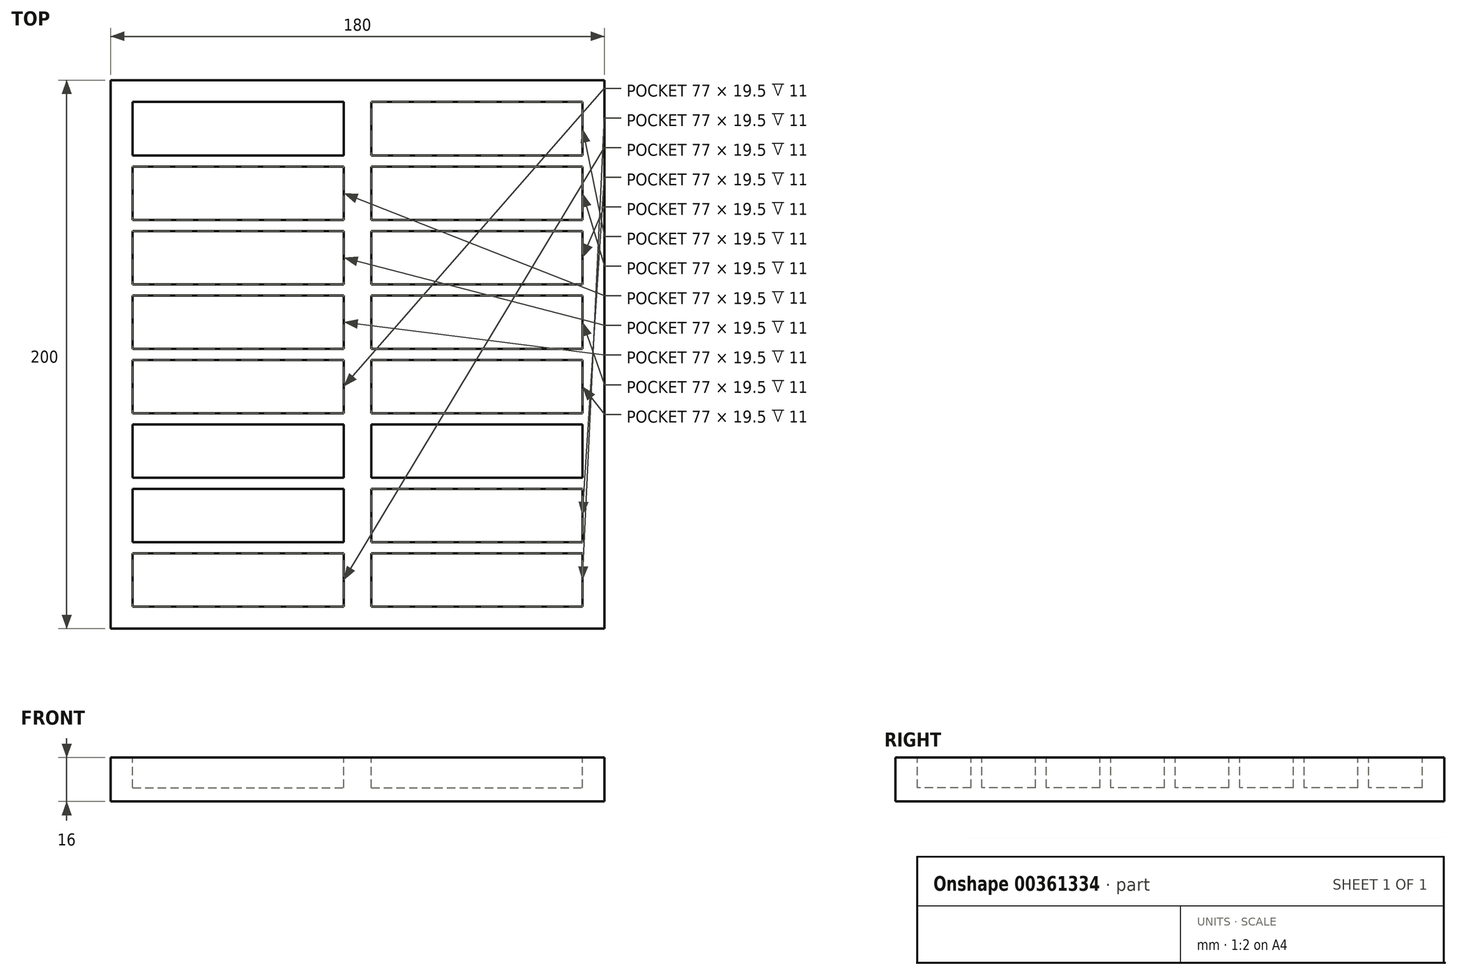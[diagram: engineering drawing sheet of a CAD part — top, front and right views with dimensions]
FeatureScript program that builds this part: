
annotation { "Feature Type Name" : "Feature", "Feature Type Description" : "" }
export const myFeature = defineFeature(function(context is Context, id is Id, definition is map)
    precondition{}
    {
        {
            var Q0;
            Q0=qCreatedBy(makeId("Top.planeOp"),FACE);
            var sketch = newSketch(context, id + "F0", { "sketchPlane" : qUnion([Q0])});
            skLineSegment(sketch, "E0.bottom", {"start": v(90, 100) * mm, "end": v(-90, 100) * mm});
            skLineSegment(sketch, "E0.top", {"start": v(90, -100) * mm, "end": v(-90, -100) * mm});
            skLineSegment(sketch, "E0.left", {"start": v(90, 100) * mm, "end": v(90, -100) * mm});
            skLineSegment(sketch, "E0.right", {"start": v(-90, 100) * mm, "end": v(-90, -100) * mm});
            skPoint(sketch, "E0.middle", {"position": v(0, 0) * mm});
            skSolve(sketch);
        }
        {
            var Q0;
            Q0 = qSketchRegion(id + "F0", true);
            extrude(context, id + "F1", {"entities" : qUnion([Q0]), "depth" : 16 * mm});
        }
        {
            var Q0;
            Q0=makeQuery(id+"F1.opExtrude","CAP_FACE",FACE,{"disambiguationData":[OSD([sQuery(id+"F0.wireOp",EDGE,"E0.bottom"),sQuery(id+"F0.wireOp",EDGE,"E0.top"),sQuery(id+"F0.wireOp",EDGE,"E0.left"),sQuery(id+"F0.wireOp",EDGE,"E0.right")])],"isStart":false});
            var sketch = newSketch(context, id + "F2", { "sketchPlane" : qUnion([Q0])});
            skLineSegment(sketch, "E1.bottom", {"start": v(-82, 92) * mm, "end": v(-5, 92) * mm});
            skLineSegment(sketch, "E1.top", {"start": v(-82, 72.5) * mm, "end": v(-5, 72.5) * mm});
            skLineSegment(sketch, "E1.left", {"start": v(-82, 92) * mm, "end": v(-82, 72.5) * mm});
            skLineSegment(sketch, "E1.right", {"start": v(-5, 92) * mm, "end": v(-5, 72.5) * mm});
            skLineSegment(sketch, "E2.0.1.0", {"start": v(-82, 49) * mm, "end": v(-5, 49) * mm});
            skLineSegment(sketch, "E2.0.1.1", {"start": v(-5, 68.5) * mm, "end": v(-5, 49) * mm});
            skLineSegment(sketch, "E2.0.1.2", {"start": v(-82, 68.5) * mm, "end": v(-5, 68.5) * mm});
            skLineSegment(sketch, "E2.0.1.3", {"start": v(-82, 68.5) * mm, "end": v(-82, 49) * mm});
            skLineSegment(sketch, "E2.0.2.0", {"start": v(-82, 25.5) * mm, "end": v(-5, 25.5) * mm});
            skLineSegment(sketch, "E2.0.2.1", {"start": v(-5, 45) * mm, "end": v(-5, 25.5) * mm});
            skLineSegment(sketch, "E2.0.2.2", {"start": v(-82, 45) * mm, "end": v(-5, 45) * mm});
            skLineSegment(sketch, "E2.0.2.3", {"start": v(-82, 45) * mm, "end": v(-82, 25.5) * mm});
            skLineSegment(sketch, "E2.0.3.0", {"start": v(-82, 2) * mm, "end": v(-5, 2) * mm});
            skLineSegment(sketch, "E2.0.3.1", {"start": v(-5, 21.5) * mm, "end": v(-5, 2) * mm});
            skLineSegment(sketch, "E2.0.3.2", {"start": v(-82, 21.5) * mm, "end": v(-5, 21.5) * mm});
            skLineSegment(sketch, "E2.0.3.3", {"start": v(-82, 21.5) * mm, "end": v(-82, 2) * mm});
            skLineSegment(sketch, "E2.0.4.0", {"start": v(-82, -21.5) * mm, "end": v(-5, -21.5) * mm});
            skLineSegment(sketch, "E2.0.4.1", {"start": v(-5, -2) * mm, "end": v(-5, -21.5) * mm});
            skLineSegment(sketch, "E2.0.4.2", {"start": v(-82, -2) * mm, "end": v(-5, -2) * mm});
            skLineSegment(sketch, "E2.0.4.3", {"start": v(-82, -2) * mm, "end": v(-82, -21.5) * mm});
            skLineSegment(sketch, "E2.0.5.0", {"start": v(-82, -45) * mm, "end": v(-5, -45) * mm});
            skLineSegment(sketch, "E2.0.5.1", {"start": v(-5, -25.5) * mm, "end": v(-5, -45) * mm});
            skLineSegment(sketch, "E2.0.5.2", {"start": v(-82, -25.5) * mm, "end": v(-5, -25.5) * mm});
            skLineSegment(sketch, "E2.0.5.3", {"start": v(-82, -25.5) * mm, "end": v(-82, -45) * mm});
            skLineSegment(sketch, "E2.0.6.0", {"start": v(-82, -68.5) * mm, "end": v(-5, -68.5) * mm});
            skLineSegment(sketch, "E2.0.6.1", {"start": v(-5, -49) * mm, "end": v(-5, -68.5) * mm});
            skLineSegment(sketch, "E2.0.6.2", {"start": v(-82, -49) * mm, "end": v(-5, -49) * mm});
            skLineSegment(sketch, "E2.0.6.3", {"start": v(-82, -49) * mm, "end": v(-82, -68.5) * mm});
            skLineSegment(sketch, "E2.0.7.0", {"start": v(-82, -92) * mm, "end": v(-5, -92) * mm});
            skLineSegment(sketch, "E2.0.7.1", {"start": v(-5, -72.5) * mm, "end": v(-5, -92) * mm});
            skLineSegment(sketch, "E2.0.7.2", {"start": v(-82, -72.5) * mm, "end": v(-5, -72.5) * mm});
            skLineSegment(sketch, "E2.0.7.3", {"start": v(-82, -72.5) * mm, "end": v(-82, -92) * mm});
            skLineSegment(sketch, "E2.1.0.0", {"start": v(5, 72.5) * mm, "end": v(82, 72.5) * mm});
            skLineSegment(sketch, "E2.1.0.1", {"start": v(82, 92) * mm, "end": v(82, 72.5) * mm});
            skLineSegment(sketch, "E2.1.0.2", {"start": v(5, 92) * mm, "end": v(82, 92) * mm});
            skLineSegment(sketch, "E2.1.0.3", {"start": v(5, 92) * mm, "end": v(5, 72.5) * mm});
            skLineSegment(sketch, "E2.1.1.0", {"start": v(5, 49) * mm, "end": v(82, 49) * mm});
            skLineSegment(sketch, "E2.1.1.1", {"start": v(82, 68.5) * mm, "end": v(82, 49) * mm});
            skLineSegment(sketch, "E2.1.1.2", {"start": v(5, 68.5) * mm, "end": v(82, 68.5) * mm});
            skLineSegment(sketch, "E2.1.1.3", {"start": v(5, 68.5) * mm, "end": v(5, 49) * mm});
            skLineSegment(sketch, "E2.1.2.0", {"start": v(5, 25.5) * mm, "end": v(82, 25.5) * mm});
            skLineSegment(sketch, "E2.1.2.1", {"start": v(82, 45) * mm, "end": v(82, 25.5) * mm});
            skLineSegment(sketch, "E2.1.2.2", {"start": v(5, 45) * mm, "end": v(82, 45) * mm});
            skLineSegment(sketch, "E2.1.2.3", {"start": v(5, 45) * mm, "end": v(5, 25.5) * mm});
            skLineSegment(sketch, "E2.1.3.0", {"start": v(5, 2) * mm, "end": v(82, 2) * mm});
            skLineSegment(sketch, "E2.1.3.1", {"start": v(82, 21.5) * mm, "end": v(82, 2) * mm});
            skLineSegment(sketch, "E2.1.3.2", {"start": v(5, 21.5) * mm, "end": v(82, 21.5) * mm});
            skLineSegment(sketch, "E2.1.3.3", {"start": v(5, 21.5) * mm, "end": v(5, 2) * mm});
            skLineSegment(sketch, "E2.1.4.0", {"start": v(5, -21.5) * mm, "end": v(82, -21.5) * mm});
            skLineSegment(sketch, "E2.1.4.1", {"start": v(82, -2) * mm, "end": v(82, -21.5) * mm});
            skLineSegment(sketch, "E2.1.4.2", {"start": v(5, -2) * mm, "end": v(82, -2) * mm});
            skLineSegment(sketch, "E2.1.4.3", {"start": v(5, -2) * mm, "end": v(5, -21.5) * mm});
            skLineSegment(sketch, "E2.1.5.0", {"start": v(5, -45) * mm, "end": v(82, -45) * mm});
            skLineSegment(sketch, "E2.1.5.1", {"start": v(82, -25.5) * mm, "end": v(82, -45) * mm});
            skLineSegment(sketch, "E2.1.5.2", {"start": v(5, -25.5) * mm, "end": v(82, -25.5) * mm});
            skLineSegment(sketch, "E2.1.5.3", {"start": v(5, -25.5) * mm, "end": v(5, -45) * mm});
            skLineSegment(sketch, "E2.1.6.0", {"start": v(5, -68.5) * mm, "end": v(82, -68.5) * mm});
            skLineSegment(sketch, "E2.1.6.1", {"start": v(82, -49) * mm, "end": v(82, -68.5) * mm});
            skLineSegment(sketch, "E2.1.6.2", {"start": v(5, -49) * mm, "end": v(82, -49) * mm});
            skLineSegment(sketch, "E2.1.6.3", {"start": v(5, -49) * mm, "end": v(5, -68.5) * mm});
            skLineSegment(sketch, "E2.1.7.0", {"start": v(5, -92) * mm, "end": v(82, -92) * mm});
            skLineSegment(sketch, "E2.1.7.1", {"start": v(82, -72.5) * mm, "end": v(82, -92) * mm});
            skLineSegment(sketch, "E2.1.7.2", {"start": v(5, -72.5) * mm, "end": v(82, -72.5) * mm});
            skLineSegment(sketch, "E2.1.7.3", {"start": v(5, -72.5) * mm, "end": v(5, -92) * mm});
            skLineSegment(sketch, "E2.direction1", {"start": v(-82, 72.5) * mm, "end": v(5, 72.5) * mm, "construction": true});
            skLineSegment(sketch, "E2.direction2", {"start": v(-82, 72.5) * mm, "end": v(-82, 49) * mm, "construction": true});
            skSolve(sketch);
        }
        {
            var Q0;
            Q0=makeQuery(id+"F2.imprint","IMPRINT",FACE,{"disambiguationData":[TD([[makeQuery(id+"F2.imprint","IMPRINT",EDGE,{"derivedFrom":sQuery(id+"F2.wireOp",EDGE,"E1.bottom")}),-1.0]])]});
            var Q1;
            Q1=makeQuery(id+"F2.imprint","IMPRINT",FACE,{"disambiguationData":[TD([[makeQuery(id+"F2.imprint","IMPRINT",EDGE,{"derivedFrom":sQuery(id+"F2.wireOp",EDGE,"E2.0.1.0")}),1.0]])]});
            var Q2;
            Q2=makeQuery(id+"F2.imprint","IMPRINT",FACE,{"disambiguationData":[TD([[makeQuery(id+"F2.imprint","IMPRINT",EDGE,{"derivedFrom":sQuery(id+"F2.wireOp",EDGE,"E2.1.1.0")}),1.0]])]});
            var Q3;
            Q3=makeQuery(id+"F2.imprint","IMPRINT",FACE,{"disambiguationData":[TD([[makeQuery(id+"F2.imprint","IMPRINT",EDGE,{"derivedFrom":sQuery(id+"F2.wireOp",EDGE,"E2.1.0.0")}),1.0]])]});
            var Q4;
            Q4=makeQuery(id+"F2.imprint","IMPRINT",FACE,{"disambiguationData":[TD([[makeQuery(id+"F2.imprint","IMPRINT",EDGE,{"derivedFrom":sQuery(id+"F2.wireOp",EDGE,"E2.1.2.0")}),1.0]])]});
            var Q5;
            Q5=makeQuery(id+"F2.imprint","IMPRINT",FACE,{"disambiguationData":[TD([[makeQuery(id+"F2.imprint","IMPRINT",EDGE,{"derivedFrom":sQuery(id+"F2.wireOp",EDGE,"E2.0.2.0")}),1.0]])]});
            var Q6;
            Q6=makeQuery(id+"F2.imprint","IMPRINT",FACE,{"disambiguationData":[TD([[makeQuery(id+"F2.imprint","IMPRINT",EDGE,{"derivedFrom":sQuery(id+"F2.wireOp",EDGE,"E2.0.3.0")}),1.0]])]});
            var Q7;
            Q7=makeQuery(id+"F2.imprint","IMPRINT",FACE,{"disambiguationData":[TD([[makeQuery(id+"F2.imprint","IMPRINT",EDGE,{"derivedFrom":sQuery(id+"F2.wireOp",EDGE,"E2.1.3.0")}),1.0]])]});
            var Q8;
            Q8=makeQuery(id+"F2.imprint","IMPRINT",FACE,{"disambiguationData":[TD([[makeQuery(id+"F2.imprint","IMPRINT",EDGE,{"derivedFrom":sQuery(id+"F2.wireOp",EDGE,"E2.1.4.0")}),1.0]])]});
            var Q9;
            Q9=makeQuery(id+"F2.imprint","IMPRINT",FACE,{"disambiguationData":[TD([[makeQuery(id+"F2.imprint","IMPRINT",EDGE,{"derivedFrom":sQuery(id+"F2.wireOp",EDGE,"E2.0.4.0")}),1.0]])]});
            var Q10;
            Q10=makeQuery(id+"F2.imprint","IMPRINT",FACE,{"disambiguationData":[TD([[makeQuery(id+"F2.imprint","IMPRINT",EDGE,{"derivedFrom":sQuery(id+"F2.wireOp",EDGE,"E2.0.5.0")}),1.0]])]});
            var Q11;
            Q11=makeQuery(id+"F2.imprint","IMPRINT",FACE,{"disambiguationData":[TD([[makeQuery(id+"F2.imprint","IMPRINT",EDGE,{"derivedFrom":sQuery(id+"F2.wireOp",EDGE,"E2.1.5.0")}),1.0]])]});
            var Q12;
            Q12=makeQuery(id+"F2.imprint","IMPRINT",FACE,{"disambiguationData":[TD([[makeQuery(id+"F2.imprint","IMPRINT",EDGE,{"derivedFrom":sQuery(id+"F2.wireOp",EDGE,"E2.0.6.0")}),1.0]])]});
            var Q13;
            Q13=makeQuery(id+"F2.imprint","IMPRINT",FACE,{"disambiguationData":[TD([[makeQuery(id+"F2.imprint","IMPRINT",EDGE,{"derivedFrom":sQuery(id+"F2.wireOp",EDGE,"E2.1.6.0")}),1.0]])]});
            var Q14;
            Q14=makeQuery(id+"F2.imprint","IMPRINT",FACE,{"disambiguationData":[TD([[makeQuery(id+"F2.imprint","IMPRINT",EDGE,{"derivedFrom":sQuery(id+"F2.wireOp",EDGE,"E2.0.7.0")}),1.0]])]});
            var Q15;
            Q15=makeQuery(id+"F2.imprint","IMPRINT",FACE,{"disambiguationData":[TD([[makeQuery(id+"F2.imprint","IMPRINT",EDGE,{"derivedFrom":sQuery(id+"F2.wireOp",EDGE,"E2.1.7.0")}),1.0]])]});
            extrude(context, id + "F3", {"entities" : qUnion([Q0, Q1, Q2, Q3, Q4, Q5, Q6, Q7, Q8, Q9, Q10, Q11, Q12, Q13, Q14, Q15]), "operationType" : NewBodyOperationType.REMOVE, "oppositeDirection" : true, "depth" : 11 * mm});
        }
    });
